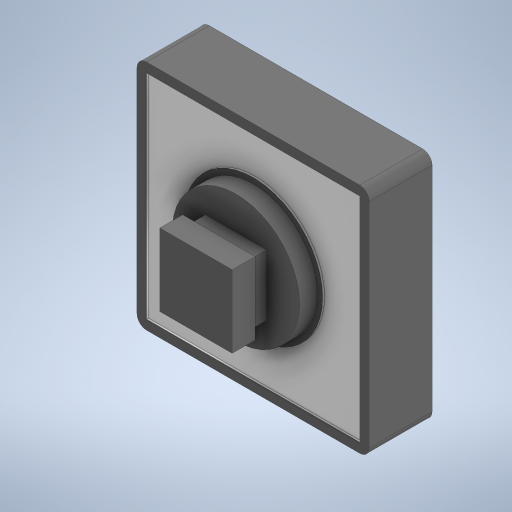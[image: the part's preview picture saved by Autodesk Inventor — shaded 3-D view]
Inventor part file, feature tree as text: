
AUTODESK INVENTOR PART (.ipt)
format: ipt  version: 2023 (Build 270158000, 158)  size: 295,936 bytes
history: native  units: mm
features: extrude x5, sketch x3, projected_geometry x2, other x1, fillet x1
ambient origin geometry x8: Origin, YZ Plane, XZ Plane, XY Plane, X Axis, Y Axis, Z Axis, Center Point
bodies: Body1 (feature_tree)
feature tree (12):
  other  "솔리드1"
  sketch  "스케치1"
  extrude  "돌출1"  Depth=12.2mm
  extrude  "돌출2"  Depth=12.2mm
  extrude  "돌출3"  Depth=6.7mm
  extrude  "돌출4"  Depth=3.2mm
  fillet  "모깎기1"  Radius=3.2mm
  extrude  "돌출5"  Depth=3.8mm
  sketch  "스케치2"
  projected_geometry  "투영된 루프1"
  sketch  "스케치3"
  projected_geometry  "투영된 루프2"
